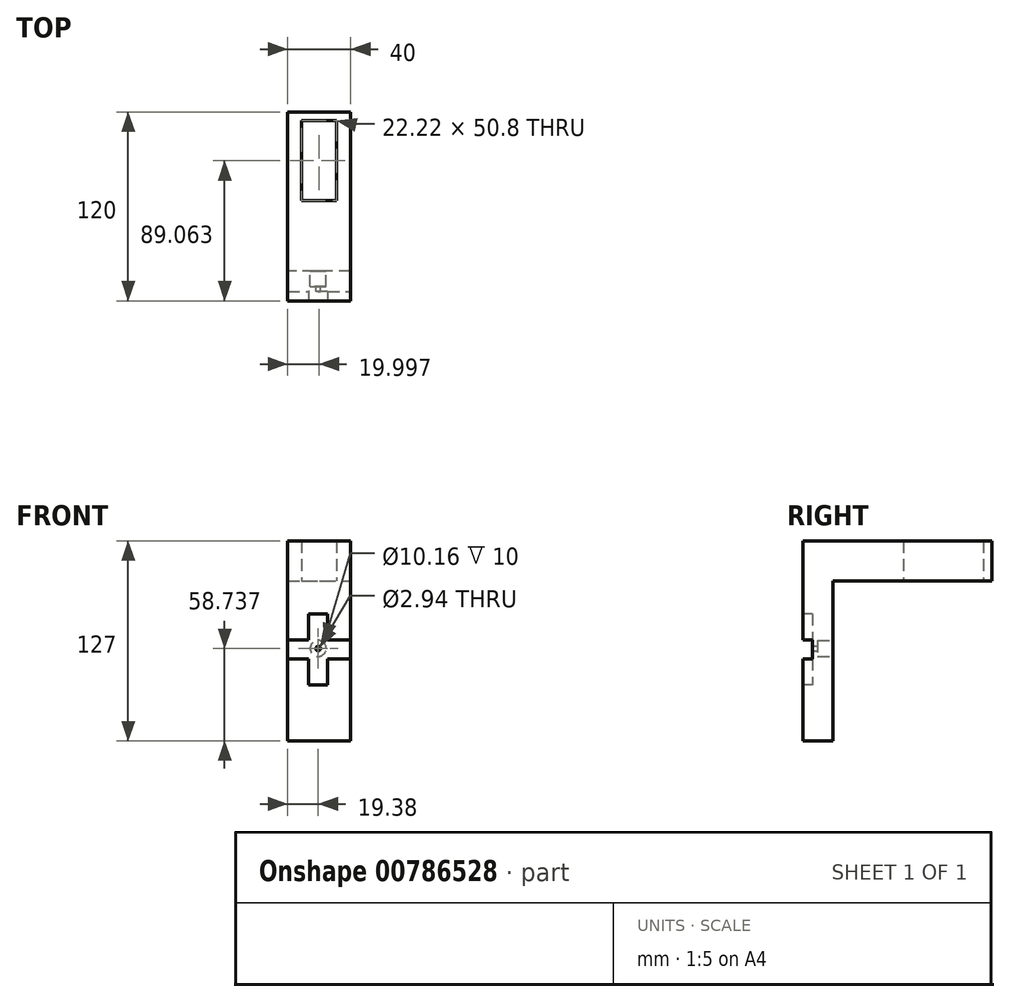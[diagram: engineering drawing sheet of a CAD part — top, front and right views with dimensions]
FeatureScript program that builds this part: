
annotation { "Feature Type Name" : "Feature", "Feature Type Description" : "" }
export const myFeature = defineFeature(function(context is Context, id is Id, definition is map)
    precondition{}
    {
        {
            var Q0;
            Q0=qCreatedBy(makeId("Top.planeOp"),FACE);
            var sketch = newSketch(context, id + "F0", { "sketchPlane" : qUnion([Q0])});
            skLineSegment(sketch, "E0.bottom", {"start": v(-19.38, 56.73) * mm, "end": v(20.62, 56.73) * mm});
            skLineSegment(sketch, "E0.top", {"start": v(-19.38, -63.27) * mm, "end": v(20.62, -63.27) * mm});
            skLineSegment(sketch, "E0.left", {"start": v(-19.38, 56.73) * mm, "end": v(-19.38, -63.27) * mm});
            skLineSegment(sketch, "E0.right", {"start": v(20.62, 56.73) * mm, "end": v(20.62, -63.27) * mm});
            skLineSegment(sketch, "E1", {"start": v(-19.38, 51.2) * mm, "end": v(20.62, 51.2) * mm});
            skLineSegment(sketch, "E2", {"start": v(-19.38, 0.4) * mm, "end": v(20.62, 0.4) * mm});
            skLineSegment(sketch, "E3", {"start": v(-19.38, -37.87) * mm, "end": v(20.62, -37.87) * mm});
            skLineSegment(sketch, "E4", {"start": v(-10.5, 51.2) * mm, "end": v(-10.5, 0) * mm});
            skLineSegment(sketch, "E5", {"start": v(11.73, 51.2) * mm, "end": v(11.73, 0) * mm});
            skSolve(sketch);
        }
        {
            var Q0;
            {var subQ6=sQuery(id+"F0.wireOp",EDGE,"E3");Q0=makeQuery(id+"F0.imprint","IMPRINT",FACE,{"disambiguationData":[TD([[makeQuery(id+"F0.imprint","IMPRINT",EDGE,{"derivedFrom":subQ6}),1.0]])]});}
            var Q1;
            {var subQ0=sQuery(id+"F0.wireOp",EDGE,"E1");var subQ1=sQuery(id+"F0.wireOp",EDGE,"E0.left");var subQ2=makeQuery(id+"F0.imprint","INTERSECT",VERTEX,{"derivedFrom":[subQ1,subQ0]});Q1=makeQuery(id+"F0.imprint","IMPRINT",FACE,{"disambiguationData":[TD([[makeQuery(id+"F0.imprint","IMPRINT",EDGE,{"disambiguationData":[TD([[subQ2,-1.0]])],"derivedFrom":subQ1}),1.0]])]});}
            var Q2;
            {var subQ0=sQuery(id+"F0.wireOp",EDGE,"E1");var subQ1=sQuery(id+"F0.wireOp",EDGE,"E0.right");var subQ2=makeQuery(id+"F0.imprint","INTERSECT",VERTEX,{"derivedFrom":[subQ1,subQ0]});Q2=makeQuery(id+"F0.imprint","IMPRINT",FACE,{"disambiguationData":[TD([[makeQuery(id+"F0.imprint","IMPRINT",EDGE,{"disambiguationData":[TD([[subQ2,-1.0]])],"derivedFrom":subQ1}),-1.0]])]});}
            var Q3;
            {var subQ1=sQuery(id+"F0.wireOp",EDGE,"E0.bottom");Q3=makeQuery(id+"F0.imprint","IMPRINT",FACE,{"disambiguationData":[TD([[makeQuery(id+"F0.imprint","IMPRINT",EDGE,{"derivedFrom":subQ1}),-1.0]])]});}
            var Q4;
            {var subQ0=sQuery(id+"F0.wireOp",EDGE,"E0.top");Q4=makeQuery(id+"F0.imprint","IMPRINT",FACE,{"disambiguationData":[TD([[makeQuery(id+"F0.imprint","IMPRINT",EDGE,{"derivedFrom":subQ0}),1.0]])]});}
            extrude(context, id + "F1", {"entities" : qUnion([Q0, Q1, Q2, Q3, Q4]), "depth" : 25.4 * mm, "offsetDistance" : 25.4 * mm});
        }
        {
            var Q0;
            Q0=makeQuery(id+"F1.opExtrude","CAP_FACE",FACE,{"disambiguationData":[OSD([sQuery(id+"F0.wireOp",EDGE,"E0.bottom"),sQuery(id+"F0.wireOp",EDGE,"E0.top"),sQuery(id+"F0.wireOp",EDGE,"E0.left"),sQuery(id+"F0.wireOp",EDGE,"E0.right"),sQuery(id+"F0.wireOp",EDGE,"E1"),sQuery(id+"F0.wireOp",EDGE,"E2"),sQuery(id+"F0.wireOp",EDGE,"E4"),sQuery(id+"F0.wireOp",EDGE,"E5")])],"isStart":true});
            var sketch = newSketch(context, id + "F2", { "sketchPlane" : qUnion([Q0])});
            skLineSegment(sketch, "E6", {"start": v(20.62, 44.22) * mm, "end": v(-19.38, 44.22) * mm});
            skSolve(sketch);
        }
        {
            var Q0;
            Q0 = qSketchRegion(id + "F2", true);
            var Q1;
            {var subQ0=sQuery(id+"F2.wireOp",EDGE,"E6");Q1=makeQuery(id+"F2.imprint","IMPRINT",FACE,{"disambiguationData":[TD([[makeQuery(id+"F2.imprint","IMPRINT",EDGE,{"derivedFrom":subQ0}),-1.0]])]});}
            extrude(context, id + "F3", {"entities" : qUnion([Q0, Q1]), "operationType" : NewBodyOperationType.ADD, "depth" : 101.6 * mm, "offsetDistance" : 25.4 * mm});
        }
        {
            var Q0;
            Q0=makeQuery(id+"F1.opExtrude","CAP_FACE",FACE,{"disambiguationData":[OSD([sQuery(id+"F0.wireOp",EDGE,"E0.bottom"),sQuery(id+"F0.wireOp",EDGE,"E0.top"),sQuery(id+"F0.wireOp",EDGE,"E0.left"),sQuery(id+"F0.wireOp",EDGE,"E0.right"),sQuery(id+"F0.wireOp",EDGE,"E1"),sQuery(id+"F0.wireOp",EDGE,"E2"),sQuery(id+"F0.wireOp",EDGE,"E4"),sQuery(id+"F0.wireOp",EDGE,"E5")])],"isStart":false});
            var sketch = newSketch(context, id + "F4", { "sketchPlane" : qUnion([Q0])});
            skLineSegment(sketch, "E7.bottom", {"start": v(-10.5, 51.2) * mm, "end": v(11.73, 51.2) * mm});
            skLineSegment(sketch, "E7.top", {"start": v(-10.5, 51.2) * mm, "end": v(11.73, 51.2) * mm});
            skLineSegment(sketch, "E7.left", {"start": v(-10.5, 51.2) * mm, "end": v(-10.5, 51.2) * mm});
            skLineSegment(sketch, "E7.right", {"start": v(11.73, 51.2) * mm, "end": v(11.73, 51.2) * mm});
            skLineSegment(sketch, "E8.top", {"start": v(-19.38, 56.73) * mm, "end": v(20.62, 56.73) * mm});
            skSolve(sketch);
        }
        {
            var Q0;
            {var subQ0=sQuery(id+"F0.wireOp",EDGE,"E0.top");Q0=makeQuery(id+"F3.boolean.opBoolean","MERGE",FACE,{"derivedFrom":[makeQuery(id+"F1.opExtrude","SWEPT_FACE",FACE,{"disambiguationData":[OSD([subQ0])]}),makeQuery(id+"F3.opExtrude","SWEPT_FACE",FACE,{"disambiguationData":[OSD([subQ0])]})]});}
            var sketch = newSketch(context, id + "F5", { "sketchPlane" : qUnion([Q0])});
            skLineSegment(sketch, "E9", {"start": v(0, 25.4) * mm, "end": v(0, -43.35) * mm});
            skLineSegment(sketch, "E10.bottom", {"start": v(-22.5, -37.35) * mm, "end": v(22.5, -37.35) * mm});
            skLineSegment(sketch, "E10.top", {"start": v(-22.5, -49.35) * mm, "end": v(22.5, -49.35) * mm});
            skLineSegment(sketch, "E10.left", {"start": v(-22.5, -37.35) * mm, "end": v(-22.5, -49.35) * mm});
            skLineSegment(sketch, "E10.right", {"start": v(22.5, -37.35) * mm, "end": v(22.5, -49.35) * mm});
            skPoint(sketch, "E10.middle", {"position": v(0, -43.35) * mm});
            skLineSegment(sketch, "E11.bottom", {"start": v(6, -20.85) * mm, "end": v(6, -65.85) * mm});
            skLineSegment(sketch, "E11.top", {"start": v(-6, -20.85) * mm, "end": v(-6, -65.85) * mm});
            skLineSegment(sketch, "E11.left", {"start": v(6, -20.85) * mm, "end": v(-6, -20.85) * mm});
            skLineSegment(sketch, "E11.right", {"start": v(6, -65.85) * mm, "end": v(-6, -65.85) * mm});
            skSolve(sketch);
        }
        {
            var Q0;
            {var subQ0=sQuery(id+"F5.wireOp",EDGE,"E10.bottom");var subQ1=sQuery(id+"F5.wireOp",EDGE,"E9");var subQ2=makeQuery(id+"F5.imprint","INTERSECT",VERTEX,{"derivedFrom":[subQ1,subQ0]});Q0=makeQuery(id+"F5.imprint","IMPRINT",FACE,{"disambiguationData":[TD([[makeQuery(id+"F5.imprint","IMPRINT",EDGE,{"disambiguationData":[TD([[subQ2,1.0]])],"derivedFrom":subQ1}),1.0]])]});}
            var Q1;
            {var subQ0=sQuery(id+"F5.wireOp",EDGE,"E10.left");Q1=makeQuery(id+"F5.imprint","IMPRINT",FACE,{"disambiguationData":[TD([[makeQuery(id+"F5.imprint","IMPRINT",EDGE,{"derivedFrom":subQ0}),1.0]])]});}
            var Q2;
            {var subQ0=sQuery(id+"F5.wireOp",EDGE,"E10.right");Q2=makeQuery(id+"F5.imprint","IMPRINT",FACE,{"disambiguationData":[TD([[makeQuery(id+"F5.imprint","IMPRINT",EDGE,{"derivedFrom":subQ0}),-1.0]])]});}
            var Q3;
            {var subQ1=sQuery(id+"F5.wireOp",EDGE,"E10.bottom");var subQ5=makeQuery(id+"F5.imprint","INTERSECT",VERTEX,{"derivedFrom":[sQuery(id+"F5.wireOp",EDGE,"E9"),subQ1]});Q3=makeQuery(id+"F5.imprint","IMPRINT",FACE,{"disambiguationData":[TD([[makeQuery(id+"F5.imprint","IMPRINT",EDGE,{"disambiguationData":[TD([[subQ5,1.0]])],"derivedFrom":subQ1}),-1.0]])]});}
            var Q4;
            {var subQ0=sQuery(id+"F5.wireOp",EDGE,"E11.bottom");var subQ1=sQuery(id+"F5.wireOp",EDGE,"E10.bottom");var subQ2=makeQuery(id+"F5.imprint","INTERSECT",VERTEX,{"derivedFrom":[subQ1,subQ0]});Q4=makeQuery(id+"F5.imprint","IMPRINT",FACE,{"disambiguationData":[TD([[makeQuery(id+"F5.imprint","IMPRINT",EDGE,{"disambiguationData":[TD([[subQ2,-1.0]])],"derivedFrom":subQ0}),1.0]])]});}
            var Q5;
            {var subQ0=sQuery(id+"F5.wireOp",EDGE,"E11.top");var subQ1=sQuery(id+"F5.wireOp",EDGE,"E10.bottom");var subQ2=makeQuery(id+"F5.imprint","INTERSECT",VERTEX,{"derivedFrom":[subQ1,subQ0]});Q5=makeQuery(id+"F5.imprint","IMPRINT",FACE,{"disambiguationData":[TD([[makeQuery(id+"F5.imprint","IMPRINT",EDGE,{"disambiguationData":[TD([[subQ2,-1.0]])],"derivedFrom":subQ0}),-1.0]])]});}
            var Q6;
            {var subQ5=sQuery(id+"F5.wireOp",EDGE,"E11.right");Q6=makeQuery(id+"F5.imprint","IMPRINT",FACE,{"disambiguationData":[TD([[makeQuery(id+"F5.imprint","IMPRINT",EDGE,{"derivedFrom":subQ5}),-1.0]])]});}
            var Q7;
            {var subQ0=sQuery(id+"F5.wireOp",EDGE,"E10.bottom");var subQ1=sQuery(id+"F5.wireOp",EDGE,"E9");var subQ2=makeQuery(id+"F5.imprint","INTERSECT",VERTEX,{"derivedFrom":[subQ1,subQ0]});Q7=makeQuery(id+"F5.imprint","IMPRINT",FACE,{"disambiguationData":[TD([[makeQuery(id+"F5.imprint","IMPRINT",EDGE,{"disambiguationData":[TD([[subQ2,1.0]])],"derivedFrom":subQ1}),-1.0]])]});}
            extrude(context, id + "F6", {"entities" : qUnion([Q0, Q1, Q2, Q3, Q4, Q5, Q6, Q7]), "operationType" : NewBodyOperationType.REMOVE, "oppositeDirection" : true, "depth" : 6 * mm, "offsetDistance" : 25.4 * mm});
        }
        {
            var Q0;
            Q0=makeQuery(id+"F3.opExtrude","SWEPT_FACE",FACE,{"disambiguationData":[OSD([sQuery(id+"F2.wireOp",EDGE,"E6")])]});
            var sketch = newSketch(context, id + "F7", { "sketchPlane" : qUnion([Q0])});
            skLineSegment(sketch, "E12", {"start": v(0, 25.9) * mm, "end": v(0, -42.86) * mm});
            skCircle(sketch, "E13", {"center": v(0, -42.86) * mm, "radius": 5.08 * mm});
            skSolve(sketch);
        }
        {
            var Q0;
            Q0 = qSketchRegion(id + "F7", true);
            extrude(context, id + "F8", {"entities" : qUnion([Q0]), "operationType" : NewBodyOperationType.REMOVE, "oppositeDirection" : true, "depth" : 10 * mm, "offsetDistance" : 25.4 * mm});
        }
        {
            var Q0;
            Q0=makeQuery(id+"F8.boolean.opBoolean","COPY",FACE,{"derivedFrom":makeQuery(id+"F8.opExtrude","CAP_FACE",FACE,{"disambiguationData":[OSD([sQuery(id+"F7.wireOp",EDGE,"E13")])],"isStart":false})});
            var sketch = newSketch(context, id + "F9", { "sketchPlane" : qUnion([Q0])});
            skCircle(sketch, "E14", {"center": v(0, -42.86) * mm, "radius": 1.47 * mm});
            skSolve(sketch);
        }
        {
            var Q0;
            Q0 = qSketchRegion(id + "F9", true);
            extrude(context, id + "F10", {"entities" : qUnion([Q0]), "operationType" : NewBodyOperationType.REMOVE, "oppositeDirection" : true, "depth" : 6 * mm, "offsetDistance" : 25.4 * mm});
        }
    });
